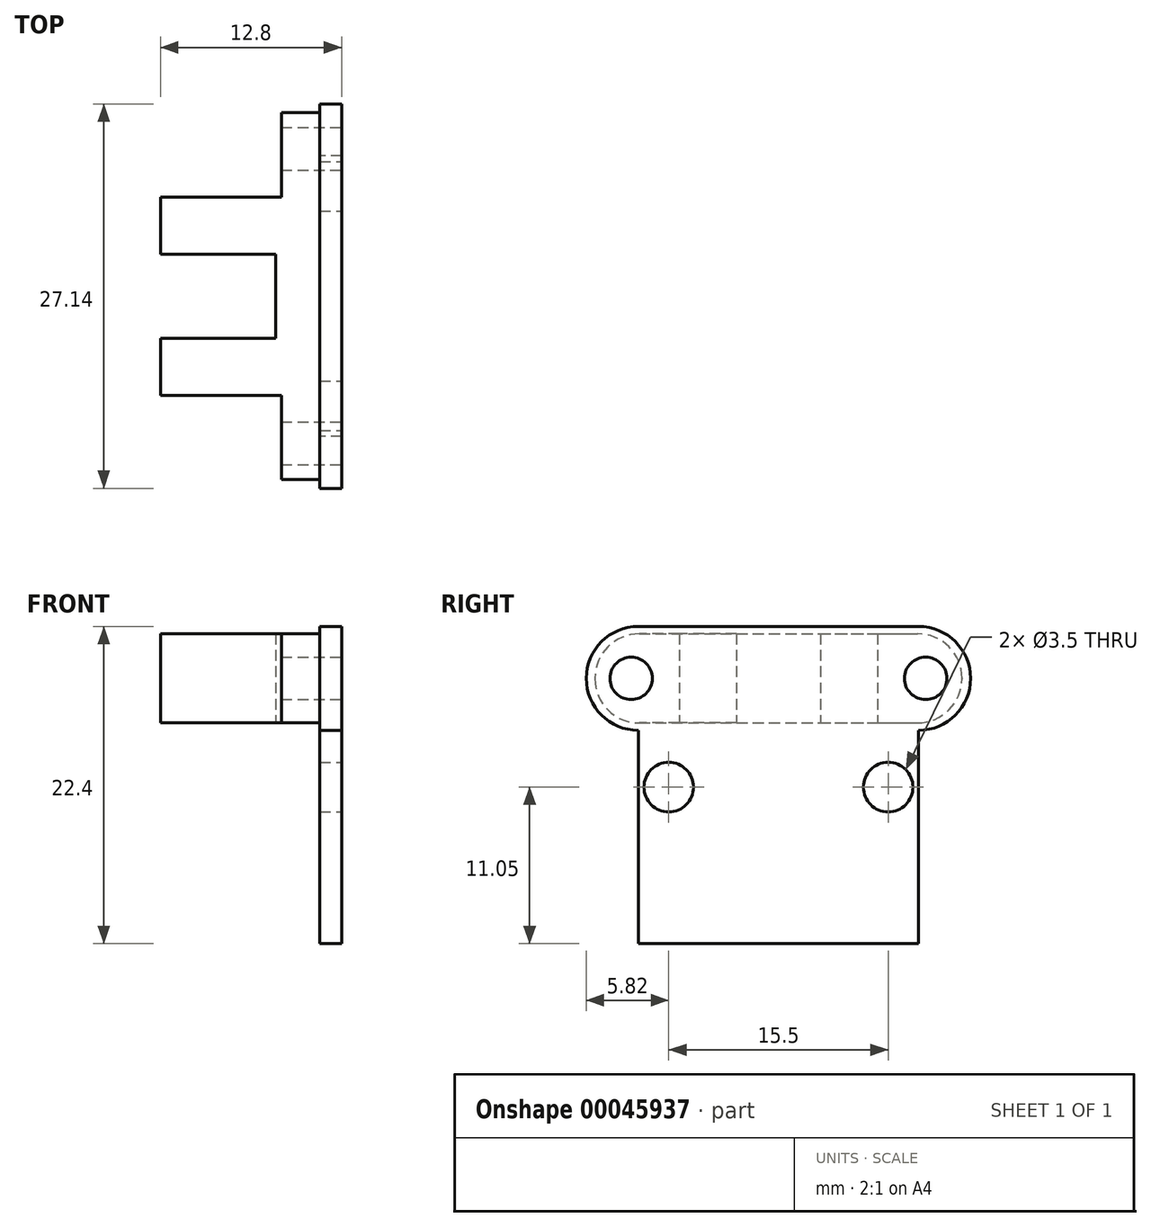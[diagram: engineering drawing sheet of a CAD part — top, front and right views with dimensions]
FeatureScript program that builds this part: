
annotation { "Feature Type Name" : "Feature", "Feature Type Description" : "" }
export const myFeature = defineFeature(function(context is Context, id is Id, definition is map)
    precondition{}
    {
        {
            var Q0;
            Q0=qCreatedBy(makeId("Top.planeOp"),FACE);
            var sketch = newSketch(context, id + "F0", { "sketchPlane" : qUnion([Q0])});
            skLineSegment(sketch, "E0", {"start": v(0, 0) * mm, "end": v(83.87, 0) * mm, "construction": true});
            skLineSegment(sketch, "E1", {"start": v(0, 0) * mm, "end": v(0, -2.97) * mm});
            skLineSegment(sketch, "E2", {"start": v(0, -2.97) * mm, "end": v(-8.13, -2.97) * mm});
            skLineSegment(sketch, "E3", {"start": v(-8.13, -2.97) * mm, "end": v(-8.13, -7) * mm});
            skLineSegment(sketch, "E4", {"start": v(-8.13, -7) * mm, "end": v(0.41, -7) * mm});
            skLineSegment(sketch, "E5", {"start": v(0.41, -7) * mm, "end": v(0.41, -12.97) * mm});
            skLineSegment(sketch, "E6", {"start": v(0.41, -12.96) * mm, "end": v(3.13, -12.96) * mm});
            skLineSegment(sketch, "E7", {"start": v(3.13, -12.96) * mm, "end": v(3.13, 0) * mm});
            skLineSegment(sketch, "E8.MirrorCS", {"start": v(0.41, 7) * mm, "end": v(0.41, 12.97) * mm});
            skLineSegment(sketch, "E9.MirrorCS", {"start": v(0.4, 12.97) * mm, "end": v(3.13, 12.97) * mm});
            skLineSegment(sketch, "E10.MirrorCS", {"start": v(0, 0) * mm, "end": v(0, 2.97) * mm});
            skLineSegment(sketch, "E11.MirrorCS", {"start": v(3.13, 12.96) * mm, "end": v(3.13, 0) * mm});
            skLineSegment(sketch, "E12.MirrorCS", {"start": v(0, 2.97) * mm, "end": v(-8.13, 2.97) * mm});
            skLineSegment(sketch, "E13.MirrorCS", {"start": v(-8.13, 7) * mm, "end": v(0.41, 7) * mm});
            skLineSegment(sketch, "E14.MirrorCS", {"start": v(-8.13, 2.97) * mm, "end": v(-8.13, 7) * mm});
            skLineSegment(sketch, "E15", {"start": v(-8.13, -2.97) * mm, "end": v(-8.13, 2.97) * mm, "construction": true});
            skSolve(sketch);
        }
        {
            var Q0;
            Q0=qSketchRegion(id+"F0",true);
            extrude(context, id + "F1", {"entities" : qUnion([Q0]), "endBound" : BoundingType.SYMMETRIC, "depth" : 6.3 * mm});
        }
        {
            var Q0;
            Q0=makeQuery(id+"F1.opExtrude","CAP_EDGE",EDGE,{"disambiguationData":[OSD([sQuery(id+"F0.wireOp",EDGE,"E9.MirrorCS")])],"isStart":false});
            var Q1;
            Q1=makeQuery(id+"F1.opExtrude","CAP_EDGE",EDGE,{"disambiguationData":[OSD([sQuery(id+"F0.wireOp",EDGE,"E9.MirrorCS")])],"isStart":true});
            var Q2;
            Q2=makeQuery(id+"F1.opExtrude","CAP_EDGE",EDGE,{"disambiguationData":[OSD([sQuery(id+"F0.wireOp",EDGE,"E6")])],"isStart":false});
            var Q3;
            Q3=makeQuery(id+"F1.opExtrude","CAP_EDGE",EDGE,{"disambiguationData":[OSD([sQuery(id+"F0.wireOp",EDGE,"E6")])],"isStart":true});
            fillet(context, id + "F2", {"entities" : qUnion([Q0, Q1, Q2, Q3]), "radius" : 3.14 * mm, "tangentPropagation" : true, "allowEdgeOverflow" : false});
        }
        {
            var Q0;
            Q0=makeQuery(id+"F1.opExtrude","SWEPT_FACE",FACE,{"disambiguationData":[OSD([sQuery(id+"F0.wireOp",EDGE,"E7"),sQuery(id+"F0.wireOp",EDGE,"E11.MirrorCS")])]});
            var sketch = newSketch(context, id + "F3", { "sketchPlane" : qUnion([Q0])});
            skLineSegment(sketch, "E16", {"start": v(0, 3.15) * mm, "end": v(0, -3.15) * mm, "construction": true});
            skLineSegment(sketch, "E17", {"start": v(-9.9, -18.73) * mm, "end": v(-9.9, -3.67) * mm});
            skArc(sketch, "E18", {"start": v(-9.9, 3.67) * mm, "mid": v(-13.57, 0) * mm, "end": v(-9.9, -3.67) * mm});
            skLineSegment(sketch, "E19.MirrorCS", {"start": v(9.9, -18.73) * mm, "end": v(9.9, -3.67) * mm});
            skArc(sketch, "E20.MirrorCS", {"start": v(9.9, 3.67) * mm, "mid": v(13.57, 0) * mm, "end": v(9.9, -3.67) * mm});
            skLineSegment(sketch, "E21", {"start": v(9.9, 3.67) * mm, "end": v(-9.9, 3.67) * mm});
            skLineSegment(sketch, "E22", {"start": v(9.9, -18.73) * mm, "end": v(-9.9, -18.73) * mm});
            skSolve(sketch);
        }
        {
            var Q0;
            Q0=makeQuery(id+"F1.opExtrude","SWEPT_FACE",FACE,{"disambiguationData":[OSD([sQuery(id+"F0.wireOp",EDGE,"E7"),sQuery(id+"F0.wireOp",EDGE,"E11.MirrorCS")])]});
            var sketch = newSketch(context, id + "F4", { "sketchPlane" : qUnion([Q0])});
            skLineSegment(sketch, "E23", {"start": v(-9.9, 0) * mm, "end": v(9.9, 0) * mm, "construction": true});
            skCircle(sketch, "E24", {"center": v(-10.4, 0) * mm, "radius": 1.5 * mm});
            skCircle(sketch, "E25.MirrorC", {"center": v(10.4, 0) * mm, "radius": 1.5 * mm});
            skCircle(sketch, "E26", {"center": v(-7.75, -7.68) * mm, "radius": 1.75 * mm});
            skCircle(sketch, "E27.MirrorC", {"center": v(7.75, -7.68) * mm, "radius": 1.75 * mm});
            skSolve(sketch);
        }
        {
            var Q0;
            Q0=qSketchRegion(id+"F3",true);
            extrude(context, id + "F5", {"entities" : qUnion([Q0]), "operationType" : NewBodyOperationType.ADD, "depth" : 1.54 * mm});
        }
        {
            var Q0;
            Q0=qSketchRegion(id+"F4",true);
            extrude(context, id + "F6", {"entities" : qUnion([Q0]), "operationType" : NewBodyOperationType.REMOVE, "endBound" : BoundingType.SYMMETRIC, "oppositeDirection" : true, "depth" : 25 * mm});
        }
    });
